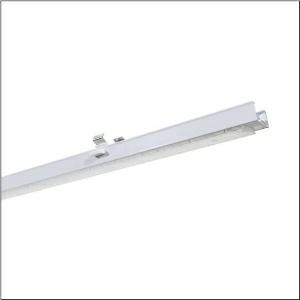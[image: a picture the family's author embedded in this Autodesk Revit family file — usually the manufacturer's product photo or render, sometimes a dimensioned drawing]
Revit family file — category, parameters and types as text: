
# Revit family: sanierungs-leuchteneinsatz_31_gen_2_51re11ma46b_d2fe
name_source: partatom
category: Lighting Fixtures
units: mm (PartAtom-declared; Revit-internal decimal feet)

## family parameters
Cut with Voids When Loaded = No
Host = Face
Light Source = No
Part Type = Normal
Room Calculation Point = No
Round Connector Dimension = Use Diameter
Shared = No

## types (1)
- --- (1 x LED, 6400 lm, 40 W, 4000K)
    Apparent Load = 40 VA
    CIE Flux Codes = 83 93 98 100 100
    Color Rendering = 80
    Color Temperature = 4000K
    Default Elevation = 1800 mm
    Description = Refurbishment luminaire insert Gen.2, luminaire insert, of extruded aluminium section, coated, traffic white (RAL 9016), length: 1.172mm, width: 91mm, height: 53mm, LED rated luminous flux: 6.400lm, light colour: 840, control gear: ON/OFF Multilumen, control gear: ECG Multilumen, with system connector: socket, mains connection: 220..240V, AC/DC, 0/50..60Hz, luminous flux adjustable on luminaire in four steps (3420/4540/5580/6630lm), connected load according to luminous flux setting (20/26/33/40W), primary light control with lens, of plastic, primary optical cover: cover, of PMMA, light emission: direct distribution, protection rating (complete): IP20, insulation class (complete): insulation class I (protective earthing), certification: CE, UKCA, permissible ambient temperature for indoor applications: -20..+40°C, packaging unit: 1 piece
    Height = 58 mm
    Lamp = 1 x LED
    Lamp Light Flux = 6400 lm
    Lamp Power = 40 W
    Lamp count = 1
    Length = 1172 mm
    Luminous efficacy = 160 lm/W
    Manufacturer = Siteco
    ModVariant = No
    Model = 51RE11MA46B
    Mounting Place = Ceiling
    Mounting Type = Pendant
    Number of Poles = 1
    OnlyDefault = Yes
    Power Factor = 1
    Product Name = Sanierungs-Leuchteneinsatz 31 Gen.2
    Product group = luminaire insert
    ProductGroupID = 902
    Protection Class = Protection class I
    Protection Degree = IP 20
    RLX_Detail_Level = 1
    RlxData = <blob elided: 19845 chars, md5=e0eb7d0b>
    Socket = socket
    Standby Power = 0 W
    System Light Flux = 6400 lm
    System Power = 40 W
    Type Comments = factory setting: luminous flux: 100 % | (ON | ON) | 300 mA
    Type Image = l_1266702.jpg
    URL = http://relux.com
    VarID = @adj_090973
    Voltage = 0 V
    Weight = 0.00 kg
    Width = 65 mm

## geometry (parser evidence)
native form markers: Blend x4, Sweep x12
no freeform markers — native parametric forms only
